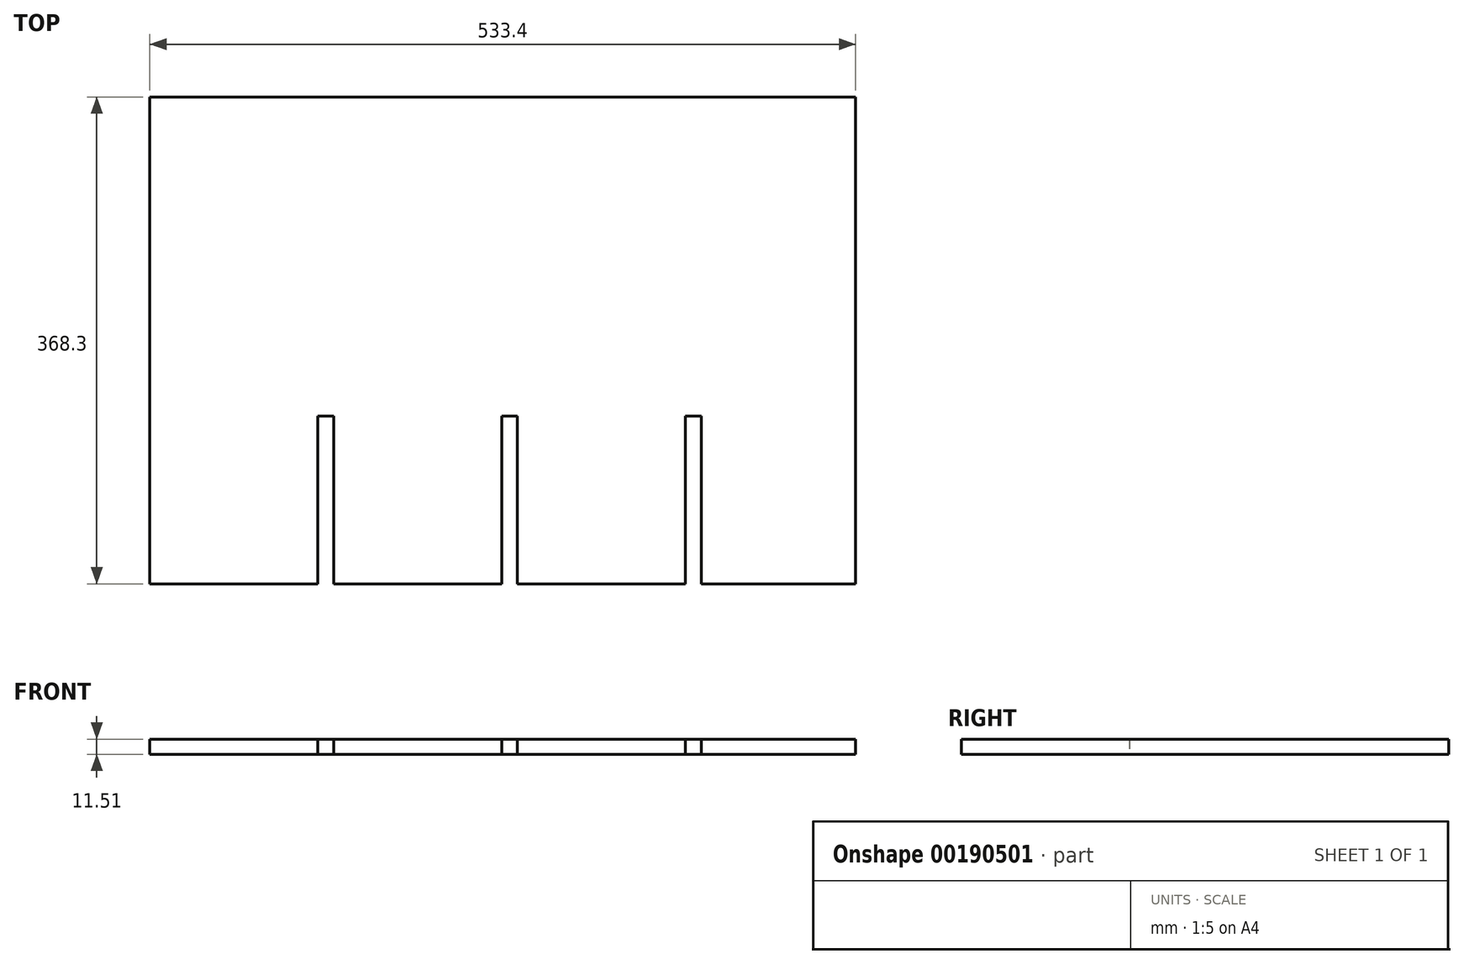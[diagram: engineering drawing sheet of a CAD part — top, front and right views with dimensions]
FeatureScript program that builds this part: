
annotation { "Feature Type Name" : "Feature", "Feature Type Description" : "" }
export const myFeature = defineFeature(function(context is Context, id is Id, definition is map)
    precondition{}
    {
        {
            var Q0;
            Q0=qCreatedBy(makeId("Top.planeOp"),FACE);
            var sketch = newSketch(context, id + "F0", { "sketchPlane" : qUnion([Q0])});
            skLineSegment(sketch, "E0.bottom", {"start": v(0, 0) * mm, "end": v(127, 0) * mm});
            skLineSegment(sketch, "E0.top", {"start": v(0, 368.3) * mm, "end": v(533.4, 368.3) * mm});
            skLineSegment(sketch, "E0.left", {"start": v(0, 0) * mm, "end": v(0, 368.3) * mm});
            skLineSegment(sketch, "E0.right", {"start": v(533.4, 0) * mm, "end": v(533.4, 368.3) * mm});
            skLineSegment(sketch, "E1", {"start": v(132.95, 0) * mm, "end": v(132.95, 247.63) * mm, "construction": true});
            skLineSegment(sketch, "E2", {"start": v(127, 0) * mm, "end": v(127, 127) * mm});
            skPoint(sketch, "E3.endSnap0", {"position": v(127, 63.5) * mm});
            skLineSegment(sketch, "E4.MirrorCS", {"start": v(138.9, 0) * mm, "end": v(138.9, 127) * mm});
            skLineSegment(sketch, "E5", {"start": v(127, 127) * mm, "end": v(138.9, 127) * mm});
            skLineSegment(sketch, "E6.trimOffspring", {"start": v(138.9, 0) * mm, "end": v(265.9, 0) * mm});
            skLineSegment(sketch, "E7.1.0.0", {"start": v(265.9, 0) * mm, "end": v(265.9, 127) * mm});
            skLineSegment(sketch, "E7.1.0.3", {"start": v(271.86, 0) * mm, "end": v(271.86, 247.63) * mm, "construction": true});
            skLineSegment(sketch, "E7.2.0.3", {"start": v(410.77, 0) * mm, "end": v(410.77, 247.63) * mm, "construction": true});
            skLineSegment(sketch, "E8.trimOffspring", {"start": v(138.9, 0) * mm, "end": v(265.9, 0) * mm, "construction": true});
            skLineSegment(sketch, "E9.trimOffspring", {"start": v(277.81, 0) * mm, "end": v(404.81, 0) * mm});
            skLineSegment(sketch, "E10.trimOffspring", {"start": v(416.72, 0) * mm, "end": v(533.4, 0) * mm});
            skLineSegment(sketch, "E11.MirrorCS", {"start": v(277.81, 0) * mm, "end": v(277.81, 127) * mm});
            skLineSegment(sketch, "E12", {"start": v(265.9, 127) * mm, "end": v(277.81, 127) * mm});
            skLineSegment(sketch, "E13", {"start": v(404.81, 0) * mm, "end": v(404.81, 127) * mm});
            skLineSegment(sketch, "E14.MirrorCS", {"start": v(416.72, 0) * mm, "end": v(416.72, 127) * mm});
            skLineSegment(sketch, "E15", {"start": v(404.81, 127) * mm, "end": v(416.72, 127) * mm});
            skSolve(sketch);
        }
        {
            var Q0;
            Q0=makeQuery(id+"F0.imprint","IMPRINT",FACE,{"disambiguationData":[TD([[makeQuery(id+"F0.imprint","IMPRINT",EDGE,{"derivedFrom":sQuery(id+"F0.wireOp",EDGE,"E0.bottom")}),1.0]])]});
            extrude(context, id + "F1", {"entities" : qUnion([Q0]), "depth" : 11.5 * mm});
        }
    });
